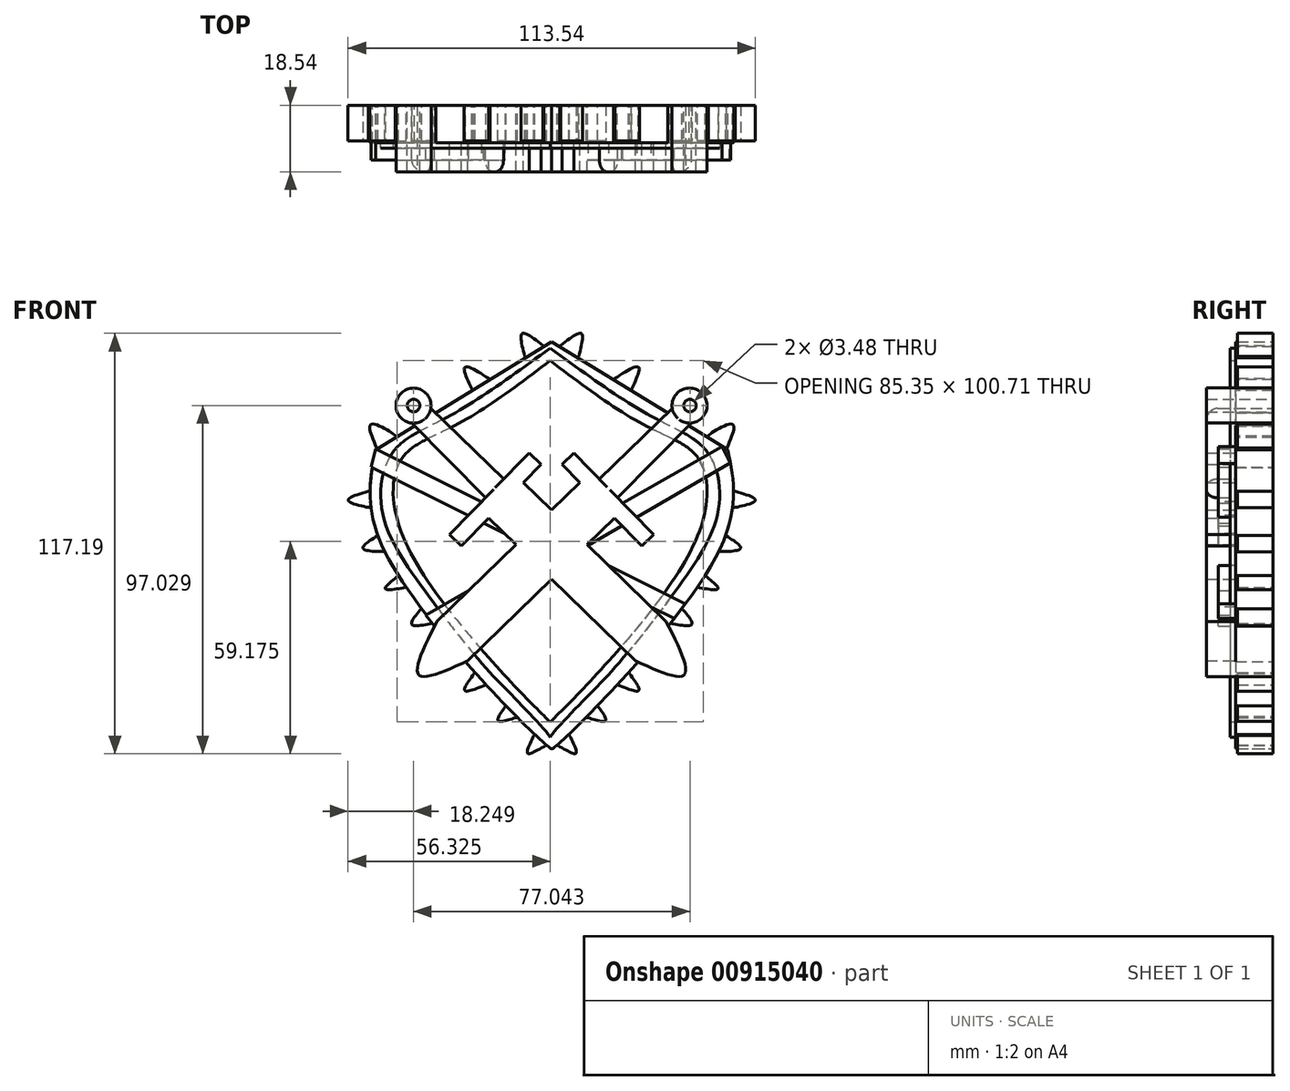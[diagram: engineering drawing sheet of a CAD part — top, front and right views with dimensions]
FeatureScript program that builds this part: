
annotation { "Feature Type Name" : "Feature", "Feature Type Description" : "" }
export const myFeature = defineFeature(function(context is Context, id is Id, definition is map)
    precondition{}
    {
        {
            var Q0;
            Q0=qCreatedBy(makeId("Front.planeOp"),FACE);
            var sketch = newSketch(context, id + "F0", { "sketchPlane" : qUnion([Q0])});
            skPoint(sketch, "E0.orphan", {"position": v(0, 50.13) * mm});
            skPoint(sketch, "E1.MirrorCS.end.orphan", {"position": v(-38.45, 32.17) * mm});
            skPoint(sketch, "E1.MirrorCS.start.orphan", {"position": v(0, -50.13) * mm});
            skPoint(sketch, "E2.end.orphan", {"position": v(38.45, 32.17) * mm});
            skLineSegment(sketch, "E3", {"start": v(-49.06, 16.15) * mm, "end": v(0, 46.28) * mm});
            skLineSegment(sketch, "E4.MirrorCS", {"start": v(49.06, 16.15) * mm, "end": v(0, 46.28) * mm});
            skFitSpline(sketch, "E5", {"points": [v(-49.06, 16.15) * mm, v(-45, -15.07) * mm, v(0, -67.18) * mm, v(0, -66.91) * mm], "startDerivative": vector(-14.07, -67.02) * mm, "endDerivative": vector(-3.38, 11) * mm});
            skFitSpline(sketch, "E6.MirrorCS", {"points": [v(49.06, 16.15) * mm, v(45, -15.07) * mm, v(0, -67.18) * mm, v(0, -66.91) * mm], "startDerivative": vector(14.07, -67.02) * mm, "endDerivative": vector(3.38, 11) * mm});
            skSolve(sketch);
        }
        {
            var Q0;
            Q0 = qSketchRegion(id + "F0", true);
            extrude(context, id + "F1", {"entities" : qUnion([Q0]), "depth" : 10.4 * mm, "offsetDistance" : 25.4 * mm});
        }
        {
            var Q0;
            Q0=qCreatedBy(makeId("Front.planeOp"),FACE);
            var sketch = newSketch(context, id + "F2", { "sketchPlane" : qUnion([Q0])});
            skCircle(sketch, "E7", {"center": v(-38.52, 28.52) * mm, "radius": 4.88 * mm});
            skLineSegment(sketch, "E8", {"start": v(-39.08, 23.67) * mm, "end": v(-18.46, 2.73) * mm});
            skLineSegment(sketch, "E9", {"start": v(-33.7, 27.73) * mm, "end": v(-13.44, 8.02) * mm});
            skLineSegment(sketch, "E10", {"start": v(-13.44, 8.02) * mm, "end": v(-28.48, -7.45) * mm});
            skLineSegment(sketch, "E11", {"start": v(-28.48, -7.45) * mm, "end": v(-25.19, -10.66) * mm});
            skLineSegment(sketch, "E12", {"start": v(-25.19, -10.66) * mm, "end": v(-3.03, 12.14) * mm});
            skLineSegment(sketch, "E13", {"start": v(-3.03, 12.14) * mm, "end": v(-6.32, 15.35) * mm});
            skLineSegment(sketch, "E14", {"start": v(-6.32, 15.35) * mm, "end": v(-13.44, 8.02) * mm});
            skLineSegment(sketch, "E15", {"start": v(-17.6, -2.85) * mm, "end": v(23.26, -42.57) * mm});
            skLineSegment(sketch, "E16", {"start": v(-7.96, 7.06) * mm, "end": v(31.87, -31.66) * mm});
            skFitSpline(sketch, "E17", {"points": [v(23.26, -42.57) * mm, v(36.92, -46.54) * mm, v(31.87, -31.66) * mm], "startDerivative": vector(37.24, -17.2) * mm, "endDerivative": vector(-19.55, 38.55) * mm});
            skCircle(sketch, "E18.MirrorC", {"center": v(38.39, 28.52) * mm, "radius": 4.88 * mm});
            skLineSegment(sketch, "E19.MirrorCS", {"start": v(33.57, 27.73) * mm, "end": v(13.3, 8.02) * mm});
            skLineSegment(sketch, "E20.MirrorCS", {"start": v(38.94, 23.67) * mm, "end": v(18.32, 2.73) * mm});
            skLineSegment(sketch, "E21.MirrorCS", {"start": v(6.19, 15.35) * mm, "end": v(13.3, 8.02) * mm});
            skLineSegment(sketch, "E22.MirrorCS", {"start": v(2.9, 12.14) * mm, "end": v(6.19, 15.35) * mm});
            skLineSegment(sketch, "E23.MirrorCS", {"start": v(25.05, -10.66) * mm, "end": v(2.9, 12.14) * mm});
            skLineSegment(sketch, "E24.MirrorCS", {"start": v(13.3, 8.02) * mm, "end": v(28.35, -7.45) * mm});
            skLineSegment(sketch, "E25.MirrorCS", {"start": v(28.35, -7.45) * mm, "end": v(25.05, -10.66) * mm});
            skLineSegment(sketch, "E26.MirrorCS", {"start": v(17.46, -2.85) * mm, "end": v(-23.4, -42.57) * mm});
            skLineSegment(sketch, "E27.MirrorCS", {"start": v(7.83, 7.06) * mm, "end": v(-32, -31.66) * mm});
            skFitSpline(sketch, "E28.MirrorCS", {"points": [v(-23.4, -42.57) * mm, v(-37.05, -46.54) * mm, v(-32, -31.66) * mm], "startDerivative": vector(-37.24, -17.2) * mm, "endDerivative": vector(19.55, 38.55) * mm});
            skCircle(sketch, "E29", {"center": v(-38.52, 28.52) * mm, "radius": 1.74 * mm});
            skCircle(sketch, "E30.MirrorC", {"center": v(38.52, 28.52) * mm, "radius": 1.74 * mm});
            skSolve(sketch);
        }
        {
            var Q0;
            Q0 = qSketchRegion(id + "F2", true);
            extrude(context, id + "F3", {"entities" : qUnion([Q0]), "operationType" : NewBodyOperationType.ADD, "depth" : 18.54 * mm, "offsetDistance" : 25.4 * mm});
        }
        {
            var Q0;
            Q0=makeQuery(id+"F3.opExtrude","CAP_EDGE",EDGE,{"disambiguationData":[OSD([sQuery(id+"F2.wireOp",EDGE,"E8")])],"isStart":false});
            var Q1;
            Q1=makeQuery(id+"F3.opExtrude","CAP_EDGE",EDGE,{"disambiguationData":[OSD([sQuery(id+"F2.wireOp",EDGE,"E9")])],"isStart":false});
            fillet(context, id + "F4", {"entities" : qUnion([Q0, Q1]), "radius" : 3.3 * mm, "tangentPropagation" : true, "allowEdgeOverflow" : false});
        }
        {
            var Q0;
            Q0=makeQuery(id+"F3.opExtrude","CAP_EDGE",EDGE,{"disambiguationData":[OSD([sQuery(id+"F2.wireOp",EDGE,"E19.MirrorCS")])],"isStart":false});
            var Q1;
            Q1=makeQuery(id+"F3.opExtrude","CAP_EDGE",EDGE,{"disambiguationData":[OSD([sQuery(id+"F2.wireOp",EDGE,"E20.MirrorCS")])],"isStart":false});
            fillet(context, id + "F5", {"entities" : qUnion([Q0, Q1]), "radius" : 3.07 * mm, "tangentPropagation" : true, "allowEdgeOverflow" : false});
        }
        {
            var Q0;
            Q0=qCreatedBy(makeId("Front.planeOp"),FACE);
            var sketch = newSketch(context, id + "F6", { "sketchPlane" : qUnion([Q0])});
            skLineSegment(sketch, "E31", {"start": v(-50.29, 11.4) * mm, "end": v(34.13, -30.8) * mm});
            skLineSegment(sketch, "E32", {"start": v(-49.06, 16.42) * mm, "end": v(37.12, -26.74) * mm});
            skLineSegment(sketch, "E33", {"start": v(47.44, 17.1) * mm, "end": v(-35.08, -29.86) * mm});
            skLineSegment(sketch, "E34", {"start": v(-31.42, -34.47) * mm, "end": v(49.47, 12.35) * mm});
            skLineSegment(sketch, "E35", {"start": v(49.47, 12.35) * mm, "end": v(49.8, 12.35) * mm});
            skLineSegment(sketch, "E36", {"start": v(-50.29, 11.4) * mm, "end": v(-49.06, 16.42) * mm});
            skLineSegment(sketch, "E37", {"start": v(47.44, 17.1) * mm, "end": v(49.8, 12.35) * mm});
            skLineSegment(sketch, "E38", {"start": v(37.12, -26.74) * mm, "end": v(34.13, -30.8) * mm});
            skLineSegment(sketch, "E39", {"start": v(-31.42, -34.47) * mm, "end": v(-35.08, -29.86) * mm});
            skSolve(sketch);
        }
        {
            var Q0;
            Q0 = qSketchRegion(id + "F6", true);
            extrude(context, id + "F7", {"entities" : qUnion([Q0]), "operationType" : NewBodyOperationType.ADD, "depth" : 15.24 * mm, "offsetDistance" : 25.4 * mm});
        }
        {
            var Q0;
            Q0=qCreatedBy(makeId("Front.planeOp"),FACE);
            var sketch = newSketch(context, id + "F8", { "sketchPlane" : qUnion([Q0])});
            skFitSpline(sketch, "E40", {"points": [v(-48.8, 16.7) * mm, v(-50.15, 23.34) * mm, v(-43.64, 20.09) * mm, v(-43.64, 19.82) * mm], "startDerivative": vector(-9.35, 21.35) * mm, "endDerivative": vector(-1.67, -2.17) * mm});
            skFitSpline(sketch, "E41", {"points": [v(-22.33, 33.25) * mm, v(-24.23, 39.22) * mm, v(-17.58, 36.1) * mm], "startDerivative": vector(-7.98, 16.87) * mm, "endDerivative": vector(17.15, -10.8) * mm});
            skFitSpline(sketch, "E42", {"points": [v(-7.53, 42.21) * mm, v(-8.21, 48.59) * mm, v(-2.51, 45.33) * mm], "startDerivative": vector(-4.52, 17.63) * mm, "endDerivative": vector(14.53, -11.33) * mm});
            skFitSpline(sketch, "E43.MirrorCS", {"points": [v(7.53, 42.21) * mm, v(8.21, 48.59) * mm, v(2.51, 45.33) * mm], "startDerivative": vector(4.52, 17.63) * mm, "endDerivative": vector(-14.53, -11.33) * mm});
            skFitSpline(sketch, "E44.MirrorCS", {"points": [v(22.33, 33.25) * mm, v(24.23, 39.22) * mm, v(17.58, 36.1) * mm], "startDerivative": vector(7.98, 16.87) * mm, "endDerivative": vector(-17.15, -10.8) * mm});
            skFitSpline(sketch, "E45.MirrorCS", {"points": [v(48.8, 16.7) * mm, v(50.15, 23.34) * mm, v(43.64, 20.09) * mm, v(43.64, 19.82) * mm], "startDerivative": vector(9.35, 21.35) * mm, "endDerivative": vector(1.67, -2.17) * mm});
            skFitSpline(sketch, "E46", {"points": [v(-51.1, 4.61) * mm, v(-56.67, 1.9) * mm, v(-50.29, 0) * mm, v(-50.15, 0) * mm], "startDerivative": vector(-20.61, -5.98) * mm, "endDerivative": vector(0.74, 0.25) * mm});
            skFitSpline(sketch, "E47", {"points": [v(-48.39, -7.6) * mm, v(-52.6, -11.27) * mm, v(-46.35, -12.22) * mm], "startDerivative": vector(-13.72, -8.95) * mm, "endDerivative": vector(17.47, -0.37) * mm});
            skFitSpline(sketch, "E48", {"points": [v(-42.69, -18.87) * mm, v(-46.35, -22.53) * mm, v(-40.51, -22.12) * mm], "startDerivative": vector(-12.14, -9.58) * mm, "endDerivative": vector(16.2, 2.94) * mm});
            skFitSpline(sketch, "E49", {"points": [v(-36.17, -27.96) * mm, v(-39.02, -32.44) * mm, v(-33.05, -32.17) * mm], "startDerivative": vector(-10.11, -11.6) * mm, "endDerivative": vector(16.1, 3.04) * mm});
            skFitSpline(sketch, "E50", {"points": [v(-21.65, -46.15) * mm, v(-24.23, -50.9) * mm, v(-18.26, -49.27) * mm], "startDerivative": vector(-9.42, -12.97) * mm, "endDerivative": vector(15.92, 6.5) * mm});
            skFitSpline(sketch, "E51", {"points": [v(-12.83, -55.24) * mm, v(-15, -59.31) * mm, v(-9.98, -58.5) * mm], "startDerivative": vector(-7.93, -10.77) * mm, "endDerivative": vector(13.46, 4.13) * mm});
            skFitSpline(sketch, "E52", {"points": [v(-4.95, -63.38) * mm, v(-6.72, -68.4) * mm, v(-1.7, -66.23) * mm], "startDerivative": vector(-6.91, -13.7) * mm, "endDerivative": vector(13.38, 7.95) * mm});
            skFitSpline(sketch, "E53.MirrorCS", {"points": [v(51.1, 4.61) * mm, v(56.67, 1.9) * mm, v(50.29, 0) * mm, v(50.15, 0) * mm], "startDerivative": vector(20.61, -5.98) * mm, "endDerivative": vector(-0.74, 0.25) * mm});
            skFitSpline(sketch, "E54.MirrorCS", {"points": [v(48.39, -7.6) * mm, v(52.6, -11.27) * mm, v(46.35, -12.22) * mm], "startDerivative": vector(13.72, -8.95) * mm, "endDerivative": vector(-17.47, -0.37) * mm});
            skFitSpline(sketch, "E55.MirrorCS", {"points": [v(42.69, -18.87) * mm, v(46.35, -22.53) * mm, v(40.51, -22.12) * mm], "startDerivative": vector(12.14, -9.58) * mm, "endDerivative": vector(-16.2, 2.94) * mm});
            skFitSpline(sketch, "E56.MirrorCS", {"points": [v(36.17, -27.96) * mm, v(39.02, -32.44) * mm, v(33.05, -32.17) * mm], "startDerivative": vector(10.11, -11.6) * mm, "endDerivative": vector(-16.1, 3.04) * mm});
            skFitSpline(sketch, "E57.MirrorCS", {"points": [v(12.83, -55.24) * mm, v(15, -59.31) * mm, v(9.98, -58.5) * mm], "startDerivative": vector(7.93, -10.77) * mm, "endDerivative": vector(-13.46, 4.13) * mm});
            skFitSpline(sketch, "E58.MirrorCS", {"points": [v(4.95, -63.38) * mm, v(6.72, -68.4) * mm, v(1.7, -66.23) * mm], "startDerivative": vector(6.91, -13.7) * mm, "endDerivative": vector(-13.38, 7.95) * mm});
            skFitSpline(sketch, "E59.MirrorCS", {"points": [v(21.65, -46.15) * mm, v(24.23, -50.9) * mm, v(18.26, -49.27) * mm], "startDerivative": vector(9.42, -12.97) * mm, "endDerivative": vector(-15.92, 6.5) * mm});
            skLineSegment(sketch, "E60", {"start": v(-22.33, 33.25) * mm, "end": v(-22.03, 32.73) * mm});
            skLineSegment(sketch, "E61", {"start": v(-17.58, 36.1) * mm, "end": v(-17.14, 35.72) * mm});
            skLineSegment(sketch, "E62", {"start": v(-2.51, 45.33) * mm, "end": v(-2.22, 44.88) * mm});
            skLineSegment(sketch, "E63", {"start": v(-7.53, 42.21) * mm, "end": v(-7.17, 41.76) * mm});
            skLineSegment(sketch, "E64", {"start": v(-43.59, 19.88) * mm, "end": v(-43.27, 19.48) * mm});
            skLineSegment(sketch, "E65", {"start": v(-48.8, 16.7) * mm, "end": v(-48.4, 16.37) * mm});
            skLineSegment(sketch, "E66", {"start": v(-51.1, 4.61) * mm, "end": v(-50.49, 4.61) * mm});
            skLineSegment(sketch, "E67", {"start": v(-21.65, -46.15) * mm, "end": v(-21.09, -45.49) * mm});
            skLineSegment(sketch, "E68", {"start": v(-9.98, -58.5) * mm, "end": v(-9.58, -58.5) * mm});
            skLineSegment(sketch, "E69", {"start": v(-12.83, -55.24) * mm, "end": v(-12.36, -54.9) * mm});
            skLineSegment(sketch, "E70", {"start": v(-4.95, -63.38) * mm, "end": v(-4.62, -62.93) * mm});
            skLineSegment(sketch, "E71", {"start": v(-1.7, -66.23) * mm, "end": v(-1.26, -65.95) * mm});
            skLineSegment(sketch, "E72", {"start": v(-1.3, -65.88) * mm, "end": v(-4.62, -62.93) * mm});
            skLineSegment(sketch, "E73", {"start": v(-9.58, -58.5) * mm, "end": v(-12.36, -54.9) * mm});
            skLineSegment(sketch, "E74", {"start": v(-18.26, -49.27) * mm, "end": v(-21.09, -45.49) * mm});
            skLineSegment(sketch, "E75", {"start": v(-33.05, -32.17) * mm, "end": v(-36.17, -27.96) * mm});
            skLineSegment(sketch, "E76", {"start": v(-50.49, 4.61) * mm, "end": v(-50.15, 0) * mm});
            skLineSegment(sketch, "E77", {"start": v(-48.4, 16.37) * mm, "end": v(-43.27, 19.48) * mm});
            skLineSegment(sketch, "E78", {"start": v(-17.14, 35.72) * mm, "end": v(-22.03, 32.73) * mm});
            skLineSegment(sketch, "E79", {"start": v(-2.22, 44.88) * mm, "end": v(-7.17, 41.76) * mm});
            skLineSegment(sketch, "E80.MirrorCS", {"start": v(2.22, 44.88) * mm, "end": v(7.17, 41.76) * mm});
            skLineSegment(sketch, "E81.MirrorCS", {"start": v(17.14, 35.72) * mm, "end": v(22.03, 32.73) * mm});
            skLineSegment(sketch, "E82.MirrorCS", {"start": v(48.4, 16.37) * mm, "end": v(43.27, 19.48) * mm});
            skLineSegment(sketch, "E83.MirrorCS", {"start": v(50.49, 4.61) * mm, "end": v(50.15, 0) * mm});
            skLineSegment(sketch, "E84", {"start": v(-48.39, -7.6) * mm, "end": v(-46.35, -12.22) * mm});
            skLineSegment(sketch, "E85", {"start": v(-42.69, -18.87) * mm, "end": v(-40.51, -22.12) * mm});
            skLineSegment(sketch, "E86.MirrorCS", {"start": v(48.39, -7.6) * mm, "end": v(46.35, -12.22) * mm});
            skLineSegment(sketch, "E87.MirrorCS", {"start": v(42.69, -18.87) * mm, "end": v(40.51, -22.12) * mm});
            skLineSegment(sketch, "E88.MirrorCS", {"start": v(33.05, -32.17) * mm, "end": v(36.17, -27.96) * mm});
            skLineSegment(sketch, "E89.MirrorCS", {"start": v(18.26, -49.27) * mm, "end": v(21.09, -45.49) * mm});
            skLineSegment(sketch, "E90.MirrorCS", {"start": v(9.58, -58.5) * mm, "end": v(12.36, -54.9) * mm});
            skLineSegment(sketch, "E91.MirrorCS", {"start": v(1.3, -65.88) * mm, "end": v(4.62, -62.93) * mm});
            skLineSegment(sketch, "E92", {"start": v(2.51, 45.33) * mm, "end": v(2.22, 44.88) * mm});
            skLineSegment(sketch, "E93", {"start": v(7.53, 42.21) * mm, "end": v(7.17, 41.76) * mm});
            skLineSegment(sketch, "E94", {"start": v(17.58, 36.1) * mm, "end": v(17.14, 35.72) * mm});
            skLineSegment(sketch, "E95", {"start": v(22.33, 33.25) * mm, "end": v(22.03, 32.73) * mm});
            skLineSegment(sketch, "E96", {"start": v(43.64, 20.09) * mm, "end": v(43.27, 19.48) * mm});
            skLineSegment(sketch, "E97", {"start": v(48.8, 16.7) * mm, "end": v(48.4, 16.37) * mm});
            skLineSegment(sketch, "E98", {"start": v(51.1, 4.61) * mm, "end": v(50.49, 4.61) * mm});
            skLineSegment(sketch, "E99", {"start": v(21.65, -46.15) * mm, "end": v(21.09, -45.49) * mm});
            skLineSegment(sketch, "E100", {"start": v(12.83, -55.24) * mm, "end": v(12.36, -54.9) * mm});
            skLineSegment(sketch, "E101", {"start": v(12.3, -54.38) * mm, "end": v(12.83, -55.24) * mm});
            skLineSegment(sketch, "E102", {"start": v(4.56, -62.78) * mm, "end": v(4.95, -63.38) * mm});
            skLineSegment(sketch, "E103", {"start": v(1.7, -66.23) * mm, "end": v(1.3, -65.88) * mm});
            skLineSegment(sketch, "E104", {"start": v(4.95, -63.38) * mm, "end": v(4.62, -62.93) * mm});
            skLineSegment(sketch, "E105", {"start": v(9.98, -58.5) * mm, "end": v(9.58, -58.5) * mm});
            skLineSegment(sketch, "E106", {"start": v(-1.26, -65.95) * mm, "end": v(-1.7, -66.23) * mm});
            skLineSegment(sketch, "E107", {"start": v(-43.64, 20.09) * mm, "end": v(-43.27, 19.48) * mm});
            skLineSegment(sketch, "E108", {"start": v(-1.3, -65.88) * mm, "end": v(-1.26, -65.95) * mm});
            skLineSegment(sketch, "E109", {"start": v(-22.03, 32.73) * mm, "end": v(-22, 32.7) * mm});
            skLineSegment(sketch, "E110", {"start": v(-22, 32.7) * mm, "end": v(-17.14, 35.72) * mm});
            skLineSegment(sketch, "E111", {"start": v(-17.16, 35.75) * mm, "end": v(-17.14, 35.72) * mm});
            skLineSegment(sketch, "E112", {"start": v(-17.16, 35.75) * mm, "end": v(-17.15, 35.75) * mm});
            skSolve(sketch);
        }
        {
            var Q0;
            Q0 = qSketchRegion(id + "F8", true);
            extrude(context, id + "F9", {"entities" : qUnion([Q0]), "operationType" : NewBodyOperationType.ADD, "depth" : 9.9 * mm, "offsetDistance" : 25.4 * mm});
        }
        {
            var Q0;
            {var subQ0=sQuery(id+"F2.wireOp",EDGE,"E17");var subQ1=sQuery(id+"F0.wireOp",EDGE,"E6.MirrorCS");var subQ4=sQuery(id+"F2.wireOp",EDGE,"E15");var subQ6=sQuery(id+"F0.wireOp",EDGE,"E5");Q0=makeQuery(id+"F3.boolean.opBoolean","SPLIT",FACE,{"disambiguationData":[TD([makeQuery(id+"F3.opExtrude","SWEPT_FACE",FACE,{"disambiguationData":[OSD([subQ4]),TDD([makeQuery(id+"F2.imprint","IMPRINT",EDGE,{"disambiguationData":[TD([[makeQuery(id+"F2.imprint","INTERSECT",VERTEX,{"derivedFrom":[subQ4,subQ0]}),1.0]])],"derivedFrom":subQ4})])]})])],"derivedFrom":makeQuery(id+"F1.opExtrude","CAP_FACE",FACE,{"disambiguationData":[OSD([sQuery(id+"F0.wireOp",EDGE,"E3"),sQuery(id+"F0.wireOp",EDGE,"E4.MirrorCS"),subQ6,subQ1])],"isStart":false})});}
            var sketch = newSketch(context, id + "F10", { "sketchPlane" : qUnion([Q0])});
            skFitSpline(sketch, "E113", {"points": [v(-0.45, 44.55) * mm, v(-29.15, 25.27) * mm, v(-44.08, 15.77) * mm, v(-47.2, -1.2) * mm, v(-35.53, -22.9) * mm, v(-18.84, -44.08) * mm, v(-7.16, -56.3) * mm, v(-0.45, -63.9) * mm, v(-0.45, -64.03) * mm], "startDerivative": vector(-164.14, -119.84) * mm, "endDerivative": vector(-3.64, -8.21) * mm});
            skFitSpline(sketch, "E114.MirrorCS", {"points": [v(-0.45, 44.55) * mm, v(28.26, 25.27) * mm, v(43.2, 15.77) * mm, v(46.31, -1.2) * mm, v(34.64, -22.9) * mm, v(17.95, -44.08) * mm, v(6.27, -56.3) * mm, v(-0.45, -63.9) * mm, v(-0.45, -64.03) * mm], "startDerivative": vector(164.14, -119.84) * mm, "endDerivative": vector(3.64, -8.21) * mm});
            skFitSpline(sketch, "E115", {"points": [v(-0.45, 41.02) * mm, v(-26.98, 22.97) * mm, v(-41.5, 14.14) * mm, v(-43.54, -1.33) * mm, v(-31.05, -25.35) * mm, v(-9.06, -51) * mm, v(-0.45, -59.69) * mm], "startDerivative": vector(-136.67, -102.94) * mm, "endDerivative": vector(60.73, -59.34) * mm});
            skFitSpline(sketch, "E116.MirrorCS", {"points": [v(-0.45, 41.02) * mm, v(26.09, 22.97) * mm, v(40.61, 14.14) * mm, v(42.65, -1.33) * mm, v(30.16, -25.35) * mm, v(8.17, -51) * mm, v(-0.45, -59.69) * mm], "startDerivative": vector(136.67, -102.94) * mm, "endDerivative": vector(-60.73, -59.34) * mm});
            skSolve(sketch);
        }
        {
            var Q0;
            Q0 = qSketchRegion(id + "F10", true);
            extrude(context, id + "F11", {"entities" : qUnion([Q0]), "depth" : 1.57 * mm, "offsetDistance" : 25.4 * mm});
        }
        {
            var Q0;
            Q0=makeQuery(id+"F11.opExtrude","SWEPT_BODY",BODY,{"disambiguationData":[OSD([sQuery(id+"F10.wireOp",EDGE,"E113"),sQuery(id+"F10.wireOp",EDGE,"E114.MirrorCS")])]});
            deleteBodies(context, id + "F12", {"entities" : qUnion([Q0])});
        }
    });
